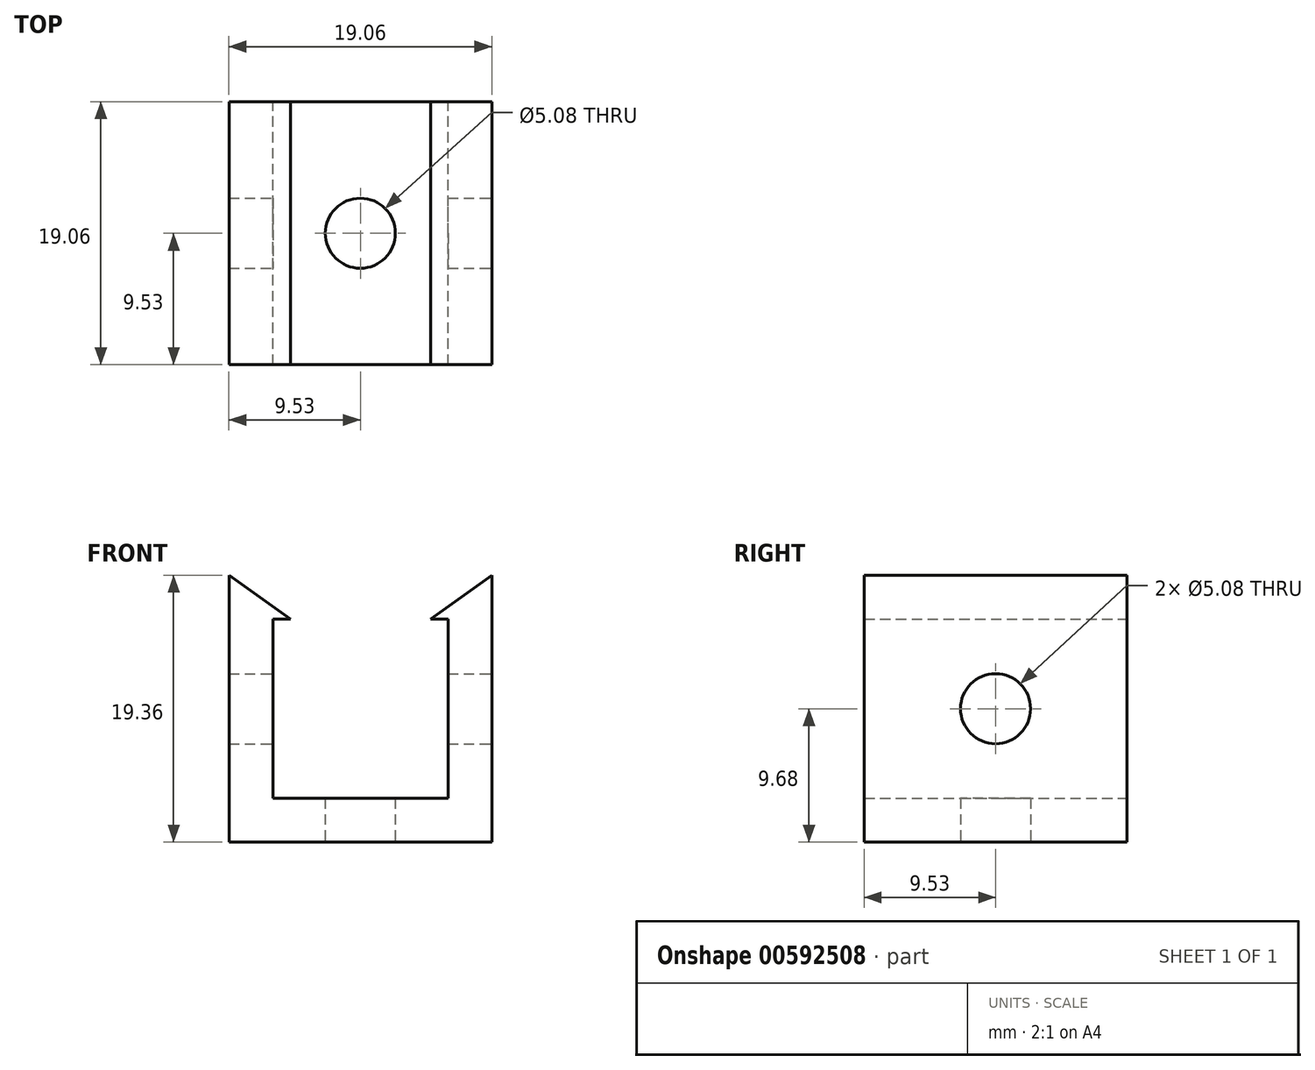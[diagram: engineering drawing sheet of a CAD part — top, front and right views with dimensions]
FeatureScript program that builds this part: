
annotation { "Feature Type Name" : "Feature", "Feature Type Description" : "" }
export const myFeature = defineFeature(function(context is Context, id is Id, definition is map)
    precondition{}
    {
        {
            var Q0;
            Q0=qCreatedBy(makeId("Front.planeOp"),FACE);
            var sketch = newSketch(context, id + "F0", { "sketchPlane" : qUnion([Q0])});
            skLineSegment(sketch, "E0.bottom", {"start": v(9.53, -9.68) * mm, "end": v(-9.53, -9.68) * mm});
            skLineSegment(sketch, "E0.left", {"start": v(9.52, -9.68) * mm, "end": v(9.52, 9.68) * mm});
            skLineSegment(sketch, "E0.right", {"start": v(-9.52, -9.68) * mm, "end": v(-9.52, 9.68) * mm});
            skPoint(sketch, "E0.middle", {"position": v(0, 0) * mm});
            skLineSegment(sketch, "E1.bottom", {"start": v(6.35, -6.5) * mm, "end": v(-6.35, -6.5) * mm});
            skLineSegment(sketch, "E1.left", {"start": v(6.35, -6.5) * mm, "end": v(6.35, 6.5) * mm});
            skLineSegment(sketch, "E1.right", {"start": v(-6.35, -6.5) * mm, "end": v(-6.35, 6.5) * mm});
            skLineSegment(sketch, "E2", {"start": v(-6.35, 6.5) * mm, "end": v(-5.08, 6.5) * mm});
            skLineSegment(sketch, "E3", {"start": v(6.35, 6.5) * mm, "end": v(5.08, 6.5) * mm});
            skLineSegment(sketch, "E4", {"start": v(5.08, 6.5) * mm, "end": v(9.52, 9.68) * mm});
            skLineSegment(sketch, "E5", {"start": v(-9.53, 9.68) * mm, "end": v(-5.08, 6.5) * mm});
            skSolve(sketch);
        }
        {
            var Q0;
            Q0 = qSketchRegion(id + "F0", true);
            extrude(context, id + "F1", {"entities" : qUnion([Q0]), "endBound" : BoundingType.SYMMETRIC, "depth" : 19.05 * mm, "offsetDistance" : 25.4 * mm});
        }
        {
            var Q0;
            Q0=makeQuery(id+"F1.opExtrude","SWEPT_FACE",FACE,{"disambiguationData":[OSD([sQuery(id+"F0.wireOp",EDGE,"E0.left")])]});
            var sketch = newSketch(context, id + "F2", { "sketchPlane" : qUnion([Q0])});
            skCircle(sketch, "E6", {"center": v(0, 0) * mm, "radius": 2.54 * mm});
            skSolve(sketch);
        }
        {
            var Q0;
            Q0 = qSketchRegion(id + "F2", true);
            extrude(context, id + "F3", {"entities" : qUnion([Q0]), "operationType" : NewBodyOperationType.REMOVE, "endBound" : BoundingType.THROUGH_ALL, "oppositeDirection" : true, "depth" : 25.4 * mm, "offsetDistance" : 25.4 * mm});
        }
        {
            var Q0;
            Q0=makeQuery(id+"F1.opExtrude","SWEPT_FACE",FACE,{"disambiguationData":[OSD([sQuery(id+"F0.wireOp",EDGE,"E0.bottom")])]});
            var sketch = newSketch(context, id + "F4", { "sketchPlane" : qUnion([Q0])});
            skCircle(sketch, "E7", {"center": v(0, 0) * mm, "radius": 2.54 * mm});
            skSolve(sketch);
        }
        {
            var Q0;
            Q0 = qSketchRegion(id + "F4", true);
            extrude(context, id + "F5", {"entities" : qUnion([Q0]), "operationType" : NewBodyOperationType.REMOVE, "endBound" : BoundingType.THROUGH_ALL, "oppositeDirection" : true, "depth" : 25.4 * mm, "offsetDistance" : 25.4 * mm});
        }
    });
